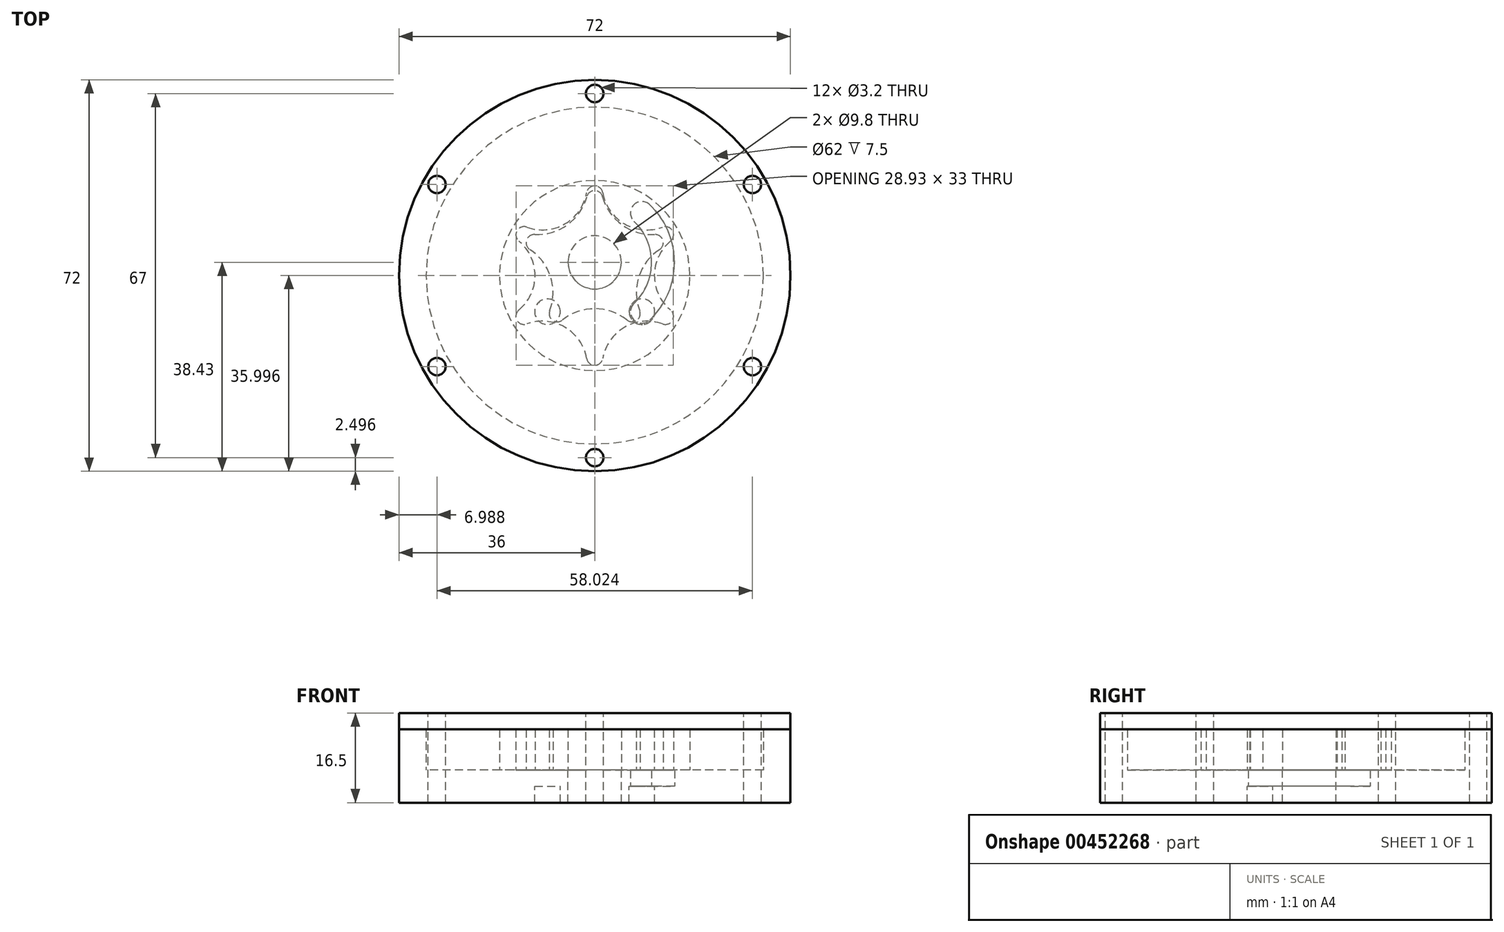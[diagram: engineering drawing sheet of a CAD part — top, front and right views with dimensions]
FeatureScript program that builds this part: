
annotation { "Feature Type Name" : "Feature", "Feature Type Description" : "" }
export const myFeature = defineFeature(function(context is Context, id is Id, definition is map)
    precondition{}
    {
        {
            var Q0;
            Q0=qCreatedBy(makeId("Top.planeOp"),FACE);
            var sketch = newSketch(context, id + "F0", { "sketchPlane" : qUnion([Q0])});
            skLineSegment(sketch, "E0", {"start": v(0, 0) * mm, "end": v(11.04, 5.1) * mm, "construction": true});
            skArc(sketch, "E1", {"start": v(1.45, 12.08) * mm, "mid": v(5.02, 6.9) * mm, "end": v(11.04, 5.1) * mm});
            skArc(sketch, "E2", {"start": v(1.45, 12.08) * mm, "mid": v(0, 13.19) * mm, "end": v(-1.45, 12.08) * mm});
            skLineSegment(sketch, "E3", {"start": v(-1.45, 12.08) * mm, "end": v(0, 0) * mm, "construction": true});
            skLineSegment(sketch, "E4", {"start": v(0, 11.69) * mm, "end": v(0, 0) * mm, "construction": true});
            skPoint(sketch, "E5.center", {"position": v(0, 0) * mm});
            skArc(sketch, "E6.1.0", {"start": v(-11.04, 5.1) * mm, "mid": v(-12.54, 4.07) * mm, "end": v(-11.94, 2.36) * mm});
            skArc(sketch, "E6.1.1", {"start": v(-11.04, 5.1) * mm, "mid": v(-5.02, 6.9) * mm, "end": v(-1.45, 12.08) * mm});
            skArc(sketch, "E6.2.0", {"start": v(-8.27, -8.92) * mm, "mid": v(-7.75, -10.67) * mm, "end": v(-5.93, -10.62) * mm});
            skArc(sketch, "E6.2.1", {"start": v(-8.27, -8.92) * mm, "mid": v(-8.12, -2.64) * mm, "end": v(-11.94, 2.36) * mm});
            skArc(sketch, "E7.3.3.0", {"start": v(5.93, -10.62) * mm, "mid": v(7.75, -10.67) * mm, "end": v(8.27, -8.92) * mm});
            skArc(sketch, "E7.4.3.0", {"start": v(5.93, -10.62) * mm, "mid": v(0, -8.54) * mm, "end": v(-5.93, -10.62) * mm});
            skArc(sketch, "E7.3.4.0", {"start": v(11.94, 2.36) * mm, "mid": v(12.54, 4.07) * mm, "end": v(11.04, 5.1) * mm});
            skArc(sketch, "E7.4.4.0", {"start": v(11.94, 2.36) * mm, "mid": v(8.12, -2.64) * mm, "end": v(8.27, -8.92) * mm});
            skCircle(sketch, "E8", {"center": v(0, 0) * mm, "radius": 4.9 * mm});
            skCircle(sketch, "E9", {"center": v(0, 0) * mm, "radius": 7.8 * mm, "construction": true});
            skSolve(sketch);
        }
        {
            var Q0;
            Q0 = qSketchRegion(id + "F0", true);
            extrude(context, id + "F1", {"entities" : qUnion([Q0]), "depth" : 7.5 * mm});
        }
        {
            var Q0;
            Q0=qCreatedBy(makeId("Top.planeOp"),FACE);
            var sketch = newSketch(context, id + "F2", { "sketchPlane" : qUnion([Q0])});
            skPoint(sketch, "E10", {"position": v(0, -2.43) * mm});
            skLineSegment(sketch, "E11", {"start": v(0, -2.43) * mm, "end": v(-1.48, 12.82) * mm, "construction": true});
            skLineSegment(sketch, "E12", {"start": v(12.47, 6.47) * mm, "end": v(0, -2.43) * mm, "construction": true});
            skArc(sketch, "E13", {"start": v(1.48, 12.82) * mm, "mid": v(0, 14.07) * mm, "end": v(-1.48, 12.82) * mm});
            skArc(sketch, "E14", {"start": v(1.48, 12.82) * mm, "mid": v(5.49, 7.07) * mm, "end": v(12.47, 6.47) * mm});
            skLineSegment(sketch, "E15", {"start": v(0, -2.43) * mm, "end": v(0, 12.57) * mm, "construction": true});
            skArc(sketch, "E16.1.0", {"start": v(-12.47, 6.47) * mm, "mid": v(-14.29, 5.82) * mm, "end": v(-13.95, 3.91) * mm});
            skArc(sketch, "E16.1.1", {"start": v(-12.47, 6.47) * mm, "mid": v(-5.49, 7.07) * mm, "end": v(-1.48, 12.82) * mm});
            skArc(sketch, "E16.2.0", {"start": v(-13.95, -8.78) * mm, "mid": v(-14.29, -10.68) * mm, "end": v(-12.47, -11.34) * mm});
            skArc(sketch, "E16.2.1", {"start": v(-13.95, -8.78) * mm, "mid": v(-10.97, -2.43) * mm, "end": v(-13.95, 3.91) * mm});
            skArc(sketch, "E17.3.3.0", {"start": v(-1.48, -17.69) * mm, "mid": v(0, -18.93) * mm, "end": v(1.48, -17.69) * mm});
            skArc(sketch, "E17.4.3.0", {"start": v(-1.48, -17.69) * mm, "mid": v(-5.49, -11.94) * mm, "end": v(-12.47, -11.34) * mm});
            skArc(sketch, "E17.3.4.0", {"start": v(12.47, -11.34) * mm, "mid": v(14.29, -10.68) * mm, "end": v(13.95, -8.78) * mm});
            skArc(sketch, "E17.4.4.0", {"start": v(12.47, -11.34) * mm, "mid": v(5.49, -11.94) * mm, "end": v(1.48, -17.69) * mm});
            skArc(sketch, "E17.3.5.0", {"start": v(13.95, 3.91) * mm, "mid": v(14.29, 5.82) * mm, "end": v(12.47, 6.47) * mm});
            skArc(sketch, "E17.4.5.0", {"start": v(13.95, 3.91) * mm, "mid": v(10.97, -2.43) * mm, "end": v(13.95, -8.78) * mm});
            skCircle(sketch, "E18", {"center": v(0, -2.43) * mm, "radius": 17.5 * mm});
            skCircle(sketch, "E19", {"center": v(0, -2.43) * mm, "radius": 10.22 * mm, "construction": true});
            skSolve(sketch);
        }
        {
            var Q0;
            Q0=makeQuery(id+"F2.imprint","IMPRINT",FACE,{"disambiguationData":[TD([[makeQuery(id+"F2.imprint","IMPRINT",EDGE,{"derivedFrom":sQuery(id+"F2.wireOp",EDGE,"E13")}),-1.0]])]});
            extrude(context, id + "F3", {"entities" : qUnion([Q0]), "operationType" : NewBodyOperationType.ADD, "depth" : 7.5 * mm});
        }
        {
            var Q0;
            Q0=qCreatedBy(makeId("Top.planeOp"),FACE);
            var sketch = newSketch(context, id + "F4", { "sketchPlane" : qUnion([Q0])});
            skLineSegment(sketch, "E20", {"start": v(0, 24.5) * mm, "end": v(0, -27.67) * mm, "construction": true});
            skCircle(sketch, "E21", {"center": v(0, -2.43) * mm, "radius": 31 * mm});
            skCircle(sketch, "E22", {"center": v(0, -2.43) * mm, "radius": 36 * mm});
            skCircle(sketch, "E23", {"center": v(0, 0) * mm, "radius": 4.9 * mm});
            skSolve(sketch);
        }
        {
            var Q0;
            Q0=makeQuery(id+"F4.imprint","IMPRINT",FACE,{"disambiguationData":[TD([[makeQuery(id+"F4.imprint","IMPRINT",EDGE,{"derivedFrom":sQuery(id+"F4.wireOp",EDGE,"E21")}),-1.0]])]});
            var Q1;
            Q1=makeQuery(id+"F4.imprint","IMPRINT",FACE,{"disambiguationData":[TD([[makeQuery(id+"F4.imprint","IMPRINT",EDGE,{"derivedFrom":sQuery(id+"F4.wireOp",EDGE,"E21")}),1.0]])]});
            extrude(context, id + "F5", {"entities" : qUnion([Q0, Q1]), "oppositeDirection" : true, "depth" : 3 * mm});
        }
        {
            var Q0;
            Q0 = qSketchRegion(id + "F4", true);
            extrude(context, id + "F6", {"entities" : qUnion([Q0]), "operationType" : NewBodyOperationType.ADD, "depth" : 7.5 * mm});
        }
        {
            var Q0;
            Q0=makeQuery(id+"F6.opExtrude","CAP_FACE",FACE,{"disambiguationData":[OSD([sQuery(id+"F4.wireOp",EDGE,"E21"),sQuery(id+"F4.wireOp",EDGE,"E22")])],"isStart":false});
            var sketch = newSketch(context, id + "F7", { "sketchPlane" : qUnion([Q0])});
            skCircle(sketch, "E24", {"center": v(0, -2.43) * mm, "radius": 36 * mm});
            skSolve(sketch);
        }
        {
            var Q0;
            Q0=makeQuery(id+"F7.imprint","IMPRINT",FACE,{"disambiguationData":[TD([[makeQuery(id+"F7.imprint","IMPRINT",EDGE,{"derivedFrom":sQuery(id+"F7.wireOp",EDGE,"E24")}),1.0]])]});
            var Q1;
            Q1=makeQuery(id+"F7.imprint","IMPRINT",FACE,{"disambiguationData":[TD([[makeQuery(id+"F7.imprint","IMPRINT",EDGE,{"derivedFrom":makeQuery(id+"F6.opExtrude","CAP_EDGE",EDGE,{"disambiguationData":[OSD([sQuery(id+"F4.wireOp",EDGE,"E21")])],"isStart":false})}),1.0]])]});
            extrude(context, id + "F8", {"entities" : qUnion([Q0, Q1]), "depth" : 3 * mm});
        }
        {
            var Q0;
            Q0=makeQuery(id+"F5.opExtrude","CAP_FACE",FACE,{"disambiguationData":[OSD([sQuery(id+"F4.wireOp",EDGE,"E22"),sQuery(id+"F4.wireOp",EDGE,"E23")])],"isStart":false});
            var sketch = newSketch(context, id + "F9", { "sketchPlane" : qUnion([Q0])});
            skLineSegment(sketch, "E25", {"start": v(0, 57.17) * mm, "end": v(0, -42.53) * mm, "construction": true});
            skArc(sketch, "E26", {"start": v(7.23, 7.56) * mm, "mid": v(10.47, 0) * mm, "end": v(7.23, -7.56) * mm});
            skArc(sketch, "E27", {"start": v(10.14, 10.6) * mm, "mid": v(14.68, 0) * mm, "end": v(10.14, -10.6) * mm});
            skArc(sketch, "E28", {"start": v(10.14, 10.6) * mm, "mid": v(7.17, 10.54) * mm, "end": v(7.23, 7.56) * mm});
            skArc(sketch, "E29", {"start": v(7.23, -7.56) * mm, "mid": v(7.17, -10.54) * mm, "end": v(10.14, -10.6) * mm});
            skSolve(sketch);
        }
        {
            var Q0;
            Q0 = qSketchRegion(id + "F9", true);
            extrude(context, id + "F10", {"entities" : qUnion([Q0]), "operationType" : NewBodyOperationType.REMOVE, "endBound" : BoundingType.UP_TO_NEXT, "oppositeDirection" : true, "depth" : 25 * mm});
        }
        {
            var Q0;
            Q0=makeQuery(id+"F5.opExtrude","CAP_FACE",FACE,{"disambiguationData":[OSD([sQuery(id+"F4.wireOp",EDGE,"E22"),sQuery(id+"F4.wireOp",EDGE,"E23")])],"isStart":false});
            var sketch = newSketch(context, id + "F11", { "sketchPlane" : qUnion([Q0])});
            skCircle(sketch, "E30.0", {"center": v(0, 2.43) * mm, "radius": 36 * mm});
            skCircle(sketch, "E31", {"center": v(8.69, 9.08) * mm, "radius": 2.35 * mm});
            skLineSegment(sketch, "E32", {"start": v(0, -49.71) * mm, "end": v(0, 59.77) * mm, "construction": true});
            skCircle(sketch, "E33.MirrorC", {"center": v(-8.69, 9.08) * mm, "radius": 2.35 * mm});
            skSolve(sketch);
        }
        {
            var Q0;
            Q0 = qSketchRegion(id + "F11", true);
            extrude(context, id + "F12", {"entities" : qUnion([Q0]), "operationType" : NewBodyOperationType.ADD, "depth" : 3 * mm});
        }
        {
            var Q0;
            Q0=makeQuery(id+"F8.opExtrude","CAP_FACE",FACE,{"disambiguationData":[OSD([sQuery(id+"F7.wireOp",EDGE,"E24")])],"isStart":false});
            var sketch = newSketch(context, id + "F13", { "sketchPlane" : qUnion([Q0])});
            skCircle(sketch, "E34", {"center": v(0, -2.43) * mm, "radius": 33.5 * mm, "construction": true});
            skLineSegment(sketch, "E35", {"start": v(0, 31.07) * mm, "end": v(0, -51.87) * mm, "construction": true});
            skCircle(sketch, "E36", {"center": v(0, 31.07) * mm, "radius": 1.6 * mm});
            skCircle(sketch, "E37.1.0", {"center": v(-29.01, 14.32) * mm, "radius": 1.6 * mm});
            skCircle(sketch, "E37.2.0", {"center": v(-29.01, -19.18) * mm, "radius": 1.6 * mm});
            skCircle(sketch, "E38.1.3.0", {"center": v(0, -35.93) * mm, "radius": 1.6 * mm});
            skCircle(sketch, "E38.1.4.0", {"center": v(29.01, -19.18) * mm, "radius": 1.6 * mm});
            skCircle(sketch, "E38.1.5.0", {"center": v(29.01, 14.32) * mm, "radius": 1.6 * mm});
            skSolve(sketch);
        }
        {
            var Q0;
            Q0 = qSketchRegion(id + "F13", true);
            extrude(context, id + "F14", {"entities" : qUnion([Q0]), "operationType" : NewBodyOperationType.REMOVE, "oppositeDirection" : true, "depth" : 25 * mm});
        }
        {
            var Q0;
            Q0=makeQuery(id+"F0.imprint","IMPRINT",FACE,{"disambiguationData":[TD([[makeQuery(id+"F0.imprint","IMPRINT",EDGE,{"derivedFrom":sQuery(id+"F0.wireOp",EDGE,"E8")}),1.0]])]});
            extrude(context, id + "F15", {"entities" : qUnion([Q0]), "operationType" : NewBodyOperationType.REMOVE, "oppositeDirection" : true, "depth" : 25 * mm, "offsetDistance" : 25 * mm});
        }
    });
